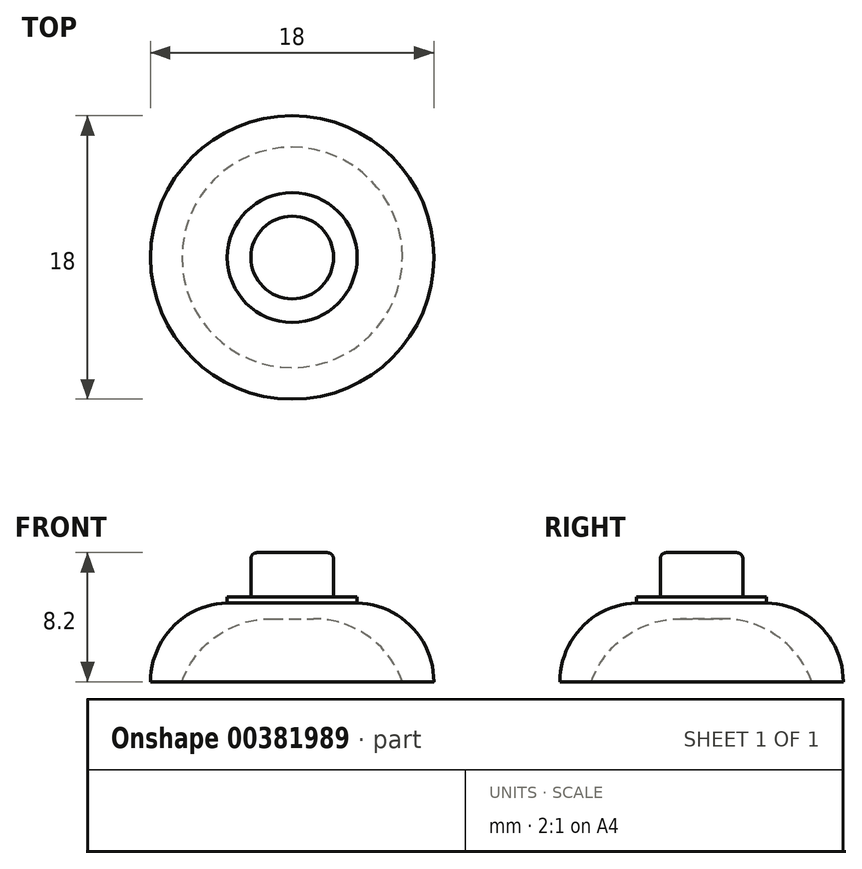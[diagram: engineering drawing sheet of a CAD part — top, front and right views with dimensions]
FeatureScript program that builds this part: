
annotation { "Feature Type Name" : "Feature", "Feature Type Description" : "" }
export const myFeature = defineFeature(function(context is Context, id is Id, definition is map)
    precondition{}
    {
        {
            var Q0;
            Q0=qCreatedBy(makeId("Top.planeOp"),FACE);
            var sketch = newSketch(context, id + "F0", { "sketchPlane" : qUnion([Q0])});
            skCircle(sketch, "E0", {"center": v(0, 0) * mm, "radius": 9 * mm});
            skCircle(sketch, "E1", {"center": v(0, 0) * mm, "radius": 4.12 * mm});
            skCircle(sketch, "E2", {"center": v(0, 0) * mm, "radius": 2.62 * mm});
            skSolve(sketch);
        }
        {
            var Q0;
            Q0=makeQuery(id+"F0.imprint","IMPRINT",FACE,{"disambiguationData":[TD([[makeQuery(id+"F0.imprint","IMPRINT",EDGE,{"derivedFrom":sQuery(id+"F0.wireOp",EDGE,"E0")}),1.0]])]});
            extrude(context, id + "F1", {"entities" : qUnion([Q0]), "depth" : 5 * mm, "offsetDistance" : 25 * mm});
        }
        {
            var Q0;
            Q0=makeQuery(id+"F0.imprint","IMPRINT",FACE,{"disambiguationData":[TD([[makeQuery(id+"F0.imprint","IMPRINT",EDGE,{"derivedFrom":sQuery(id+"F0.wireOp",EDGE,"E1")}),1.0]])]});
            extrude(context, id + "F2", {"entities" : qUnion([Q0]), "operationType" : NewBodyOperationType.ADD, "depth" : 5.4 * mm, "offsetDistance" : 25 * mm});
        }
        {
            var Q0;
            Q0=makeQuery(id+"F0.imprint","IMPRINT",FACE,{"disambiguationData":[TD([[makeQuery(id+"F0.imprint","IMPRINT",EDGE,{"derivedFrom":sQuery(id+"F0.wireOp",EDGE,"E2")}),1.0]])]});
            extrude(context, id + "F3", {"entities" : qUnion([Q0]), "operationType" : NewBodyOperationType.ADD, "depth" : (5.8 + 2.4) * mm, "offsetDistance" : 25 * mm});
        }
        {
            var Q0;
            {var subQ0=sQuery(id+"F0.wireOp",EDGE,"E2");var subQ1=sQuery(id+"F0.wireOp",EDGE,"E1");Q0=makeQuery(id+"F3.boolean.opBoolean","MERGE",FACE,{"derivedFrom":[makeQuery(id+"F2.boolean.opBoolean","MERGE",FACE,{"derivedFrom":[makeQuery(id+"F1.opExtrude","CAP_FACE",FACE,{"disambiguationData":[OSD([sQuery(id+"F0.wireOp",EDGE,"E0"),subQ1])],"isStart":true}),makeQuery(id+"F2.opExtrude","CAP_FACE",FACE,{"disambiguationData":[OSD([subQ1,subQ0])],"isStart":true})]}),makeQuery(id+"F3.opExtrude","CAP_FACE",FACE,{"disambiguationData":[OSD([subQ0])],"isStart":true})]});}
            var sketch = newSketch(context, id + "F4", { "sketchPlane" : qUnion([Q0])});
            skCircle(sketch, "E3.0", {"center": v(0, 0) * mm, "radius": 7 * mm});
            skSolve(sketch);
        }
        {
            var Q0;
            Q0=makeQuery(id+"F4.imprint","IMPRINT",FACE,{"disambiguationData":[TD([[makeQuery(id+"F4.imprint","IMPRINT",EDGE,{"derivedFrom":sQuery(id+"F4.wireOp",EDGE,"E3.0")}),1.0]])]});
            extrude(context, id + "F5", {"entities" : qUnion([Q0]), "operationType" : NewBodyOperationType.REMOVE, "oppositeDirection" : true, "depth" : 4 * mm, "offsetDistance" : 25 * mm});
        }
        {
            var Q0;
            Q0=makeQuery(id+"F5.boolean.opBoolean","COPY",EDGE,{"derivedFrom":makeQuery(id+"F5.opExtrude","CAP_EDGE",EDGE,{"disambiguationData":[OSD([sQuery(id+"F4.wireOp",EDGE,"E3.0")])],"isStart":false})});
            fillet(context, id + "F6", {"entities" : qUnion([Q0]), "radius" : 6 * mm, "tangentPropagation" : true, "allowEdgeOverflow" : false});
        }
        {
            var Q0;
            Q0=makeQuery(id+"F1.opExtrude","CAP_EDGE",EDGE,{"disambiguationData":[OSD([sQuery(id+"F0.wireOp",EDGE,"E0")])],"isStart":false});
            fillet(context, id + "F7", {"entities" : qUnion([Q0]), "radius" : 5 * mm, "tangentPropagation" : true, "allowEdgeOverflow" : false});
        }
        {
            var Q0;
            Q0=makeQuery(id+"F3.opExtrude","CAP_EDGE",EDGE,{"disambiguationData":[OSD([sQuery(id+"F0.wireOp",EDGE,"E2")])],"isStart":false});
            fillet(context, id + "F8", {"entities" : qUnion([Q0]), "radius" : .4 * mm, "tangentPropagation" : true, "allowEdgeOverflow" : false});
        }
    });
